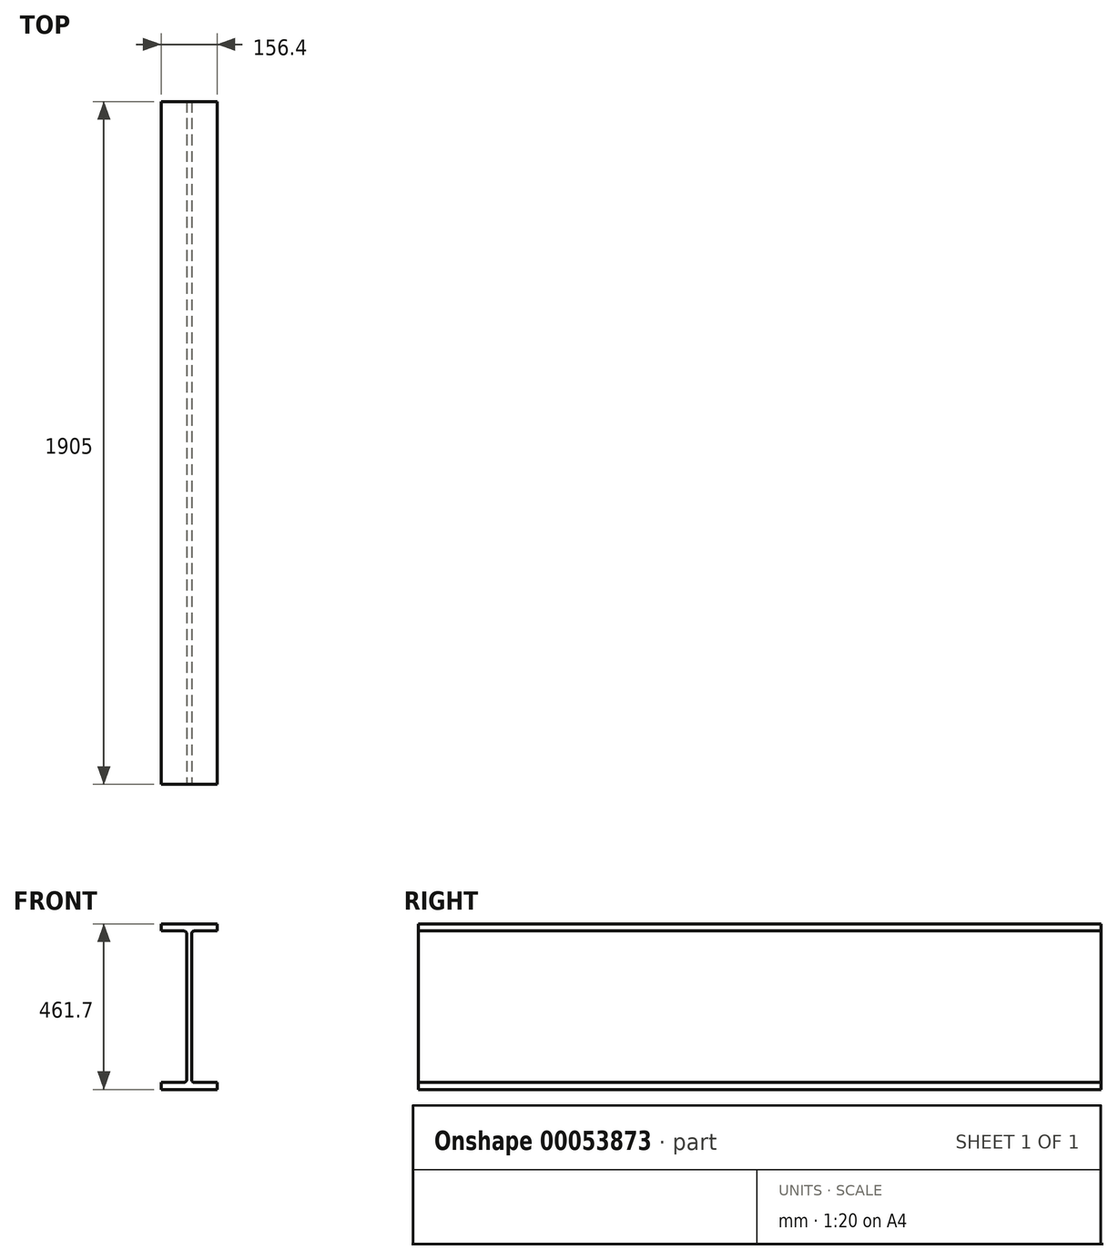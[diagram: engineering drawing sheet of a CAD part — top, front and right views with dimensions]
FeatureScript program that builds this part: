
annotation { "Feature Type Name" : "Feature", "Feature Type Description" : "" }
export const myFeature = defineFeature(function(context is Context, id is Id, definition is map)
    precondition{}
    {
        {
            var Q0;
            Q0=qCreatedBy(makeId("Front.planeOp"),FACE);
            var sketch = newSketch(context, id + "F0", { "sketchPlane" : qUnion([Q0])});
            skLineSegment(sketch, "E0.0", {"start": v(-14.75, 211.35) * mm, "end": v(-78.2, 211.35) * mm});
            skArc(sketch, "E0.1", {"start": v(-6.8, 203.4) * mm, "mid": v(-9.13, 209.02) * mm, "end": v(-14.75, 211.35) * mm});
            skLineSegment(sketch, "E0.2", {"start": v(-6.8, -203.4) * mm, "end": v(-6.8, 203.4) * mm});
            skArc(sketch, "E0.3", {"start": v(-14.75, -211.35) * mm, "mid": v(-9.13, -209.02) * mm, "end": v(-6.8, -203.4) * mm});
            skLineSegment(sketch, "E0.4", {"start": v(-78.2, -211.35) * mm, "end": v(-14.75, -211.35) * mm});
            skArc(sketch, "E0.5", {"start": v(14.75, 211.35) * mm, "mid": v(9.13, 209.02) * mm, "end": v(6.8, 203.4) * mm});
            skLineSegment(sketch, "E0.6", {"start": v(78.2, 211.35) * mm, "end": v(14.75, 211.35) * mm});
            skLineSegment(sketch, "E0.7", {"start": v(78.2, 230.85) * mm, "end": v(78.2, 211.35) * mm});
            skLineSegment(sketch, "E0.8", {"start": v(-78.2, 230.85) * mm, "end": v(78.2, 230.85) * mm});
            skLineSegment(sketch, "E0.9", {"start": v(6.8, 203.4) * mm, "end": v(6.8, -203.4) * mm});
            skArc(sketch, "E0.10", {"start": v(6.8, -203.4) * mm, "mid": v(9.13, -209.02) * mm, "end": v(14.75, -211.35) * mm});
            skLineSegment(sketch, "E0.11", {"start": v(14.75, -211.35) * mm, "end": v(78.2, -211.35) * mm});
            skLineSegment(sketch, "E0.12", {"start": v(78.2, -211.35) * mm, "end": v(78.2, -230.85) * mm});
            skLineSegment(sketch, "E0.13", {"start": v(78.2, -230.85) * mm, "end": v(-78.2, -230.85) * mm});
            skLineSegment(sketch, "E0.14", {"start": v(-78.2, 211.35) * mm, "end": v(-78.2, 230.85) * mm});
            skLineSegment(sketch, "E0.15", {"start": v(-78.2, -230.85) * mm, "end": v(-78.2, -211.35) * mm});
            skLineSegment(sketch, "E1", {"start": v(157.5, 279.43) * mm, "end": v(157.5, -255.95) * mm});
            skLineSegment(sketch, "E2.MirrorCS", {"start": v(393.2, 230.85) * mm, "end": v(236.8, 230.85) * mm});
            skLineSegment(sketch, "E3.MirrorCS", {"start": v(236.8, 230.85) * mm, "end": v(236.8, 211.35) * mm});
            skLineSegment(sketch, "E4.MirrorCS", {"start": v(236.8, 211.35) * mm, "end": v(300.25, 211.35) * mm});
            skArc(sketch, "E5.MirrorCS", {"start": v(300.25, 211.35) * mm, "mid": v(305.87, 209.02) * mm, "end": v(308.2, 203.4) * mm});
            skArc(sketch, "E6.MirrorCS", {"start": v(321.8, 203.4) * mm, "mid": v(324.13, 209.02) * mm, "end": v(329.75, 211.35) * mm});
            skLineSegment(sketch, "E7.MirrorCS", {"start": v(329.75, 211.35) * mm, "end": v(393.2, 211.35) * mm});
            skLineSegment(sketch, "E8.MirrorCS", {"start": v(321.8, -203.4) * mm, "end": v(321.8, 203.4) * mm});
            skLineSegment(sketch, "E9.MirrorCS", {"start": v(308.2, 203.4) * mm, "end": v(308.2, -203.4) * mm});
            skArc(sketch, "E10.MirrorCS", {"start": v(329.75, -211.35) * mm, "mid": v(324.13, -209.02) * mm, "end": v(321.8, -203.4) * mm});
            skArc(sketch, "E11.MirrorCS", {"start": v(308.2, -203.4) * mm, "mid": v(305.87, -209.02) * mm, "end": v(300.25, -211.35) * mm});
            skLineSegment(sketch, "E12.MirrorCS", {"start": v(300.25, -211.35) * mm, "end": v(236.8, -211.35) * mm});
            skLineSegment(sketch, "E13.MirrorCS", {"start": v(236.8, -230.85) * mm, "end": v(393.2, -230.85) * mm});
            skLineSegment(sketch, "E14.MirrorCS", {"start": v(236.8, -211.35) * mm, "end": v(236.8, -230.85) * mm});
            skLineSegment(sketch, "E15.MirrorCS", {"start": v(393.2, -230.85) * mm, "end": v(393.2, -211.35) * mm});
            skLineSegment(sketch, "E16.MirrorCS", {"start": v(393.2, -211.35) * mm, "end": v(329.75, -211.35) * mm});
            skLineSegment(sketch, "E17.MirrorCS", {"start": v(393.2, 211.35) * mm, "end": v(393.2, 230.85) * mm});
            skSolve(sketch);
        }
        {
            var Q0;
            Q0=makeQuery(id+"F0.imprint","IMPRINT",FACE,{"disambiguationData":[TD([[makeQuery(id+"F0.imprint","IMPRINT",EDGE,{"derivedFrom":sQuery(id+"F0.wireOp",EDGE,"E2.MirrorCS")}),1.0]])]});
            extrude(context, id + "F1", {"entities" : qUnion([Q0]), "oppositeDirection" : true, "depth" : 1905 * mm});
        }
    });
